# Revit family: Valve-Diverter-Waterworks-Universal-Two_Way
name_source: partatom
category: Pipe Accessories
revit_build: Autodesk Revit MEP 2014 (Build: 20140709_2115(x64)
units: mm (PartAtom-declared; Revit-internal decimal feet)

## types (2) — shared parameters
Assembly Code = D2010
Certification IAPMO = Yes
Certification State of MA = Yes
Certification cUPC = Yes
Description = Universal Two Way Diverter Valve for Thermostatic Shower Systems
Finish = Metal - Waterworks - Unfinished
Fittings Hole Diameter = 0' - 2 1/2"
Handshower Outlet Connection = Outlet - Female NPT
Keynote = 22 40 00
Length = 0' - 3"
Manufacturer = Waterworks
Mixed Water Inlet Connection = Intlet - Female NPT
Outlet Connection Diameter = 0' - 0 1/2"
Pressure = 45.00 psi
Product Documentation Link = http://assets.waterworks.com
Product Page URL = http://www.waterworks.com
Showerhead Outlet Connection = Outlet - Female NPT
Showerhead Outlet Diameter = 0' - 0 1/2"
URL = http://www.waterworks.com
Version = 2014 - v1.0a
Warranty = http://www.waterworks.com
Water Pressure = Max: 85psi / Min: 20psi / Recommended: 45psi
‌Installation Requirements or Notes = Valve rough-in depth is measured from the centerline of the inlets to the surface of the finished wall and varies depending on the trim and thermostatic valve being used. Refer to the valve Installation Guidelines for rough-in depth dimension information.

## per-type parameters (varying)
| type | 1/2" Inlet | 3/4" Inlet | Code Compliance | Constraint | Depth | Height | Mixed Water Inlet Diameter | Model | Model SKU | Product Name |
| Thermostatic Shower Systems | No | Yes | Code # GUSV14: Complies with ASME A112.18.1/CSA B125. Certified with the State of MA | 1 | 0' - 6 1/2" | 0' - 3 13/16" | 0' - 0 3/4" | GUDV14 | 26-79186-91093 | Universal Two Way Diverter Valve for Thermostatic Shower Systems |
| Pressure Balance Shower Systems | Yes | No | Code # GUSV23: Complies with ASME A112.18.1/CSA B125. Certified with the State of MA | 2 | 0' - 6 3/8" | 0' - 3 5/8" | 0' - 0 1/2" | GUDV23 | 26-13288-17225 | Universal Two Way Diverter Valve for Pressure Balance Shower Systems |

## geometry (parser evidence)
native form markers: Sweep x6
no freeform markers — native parametric forms only
